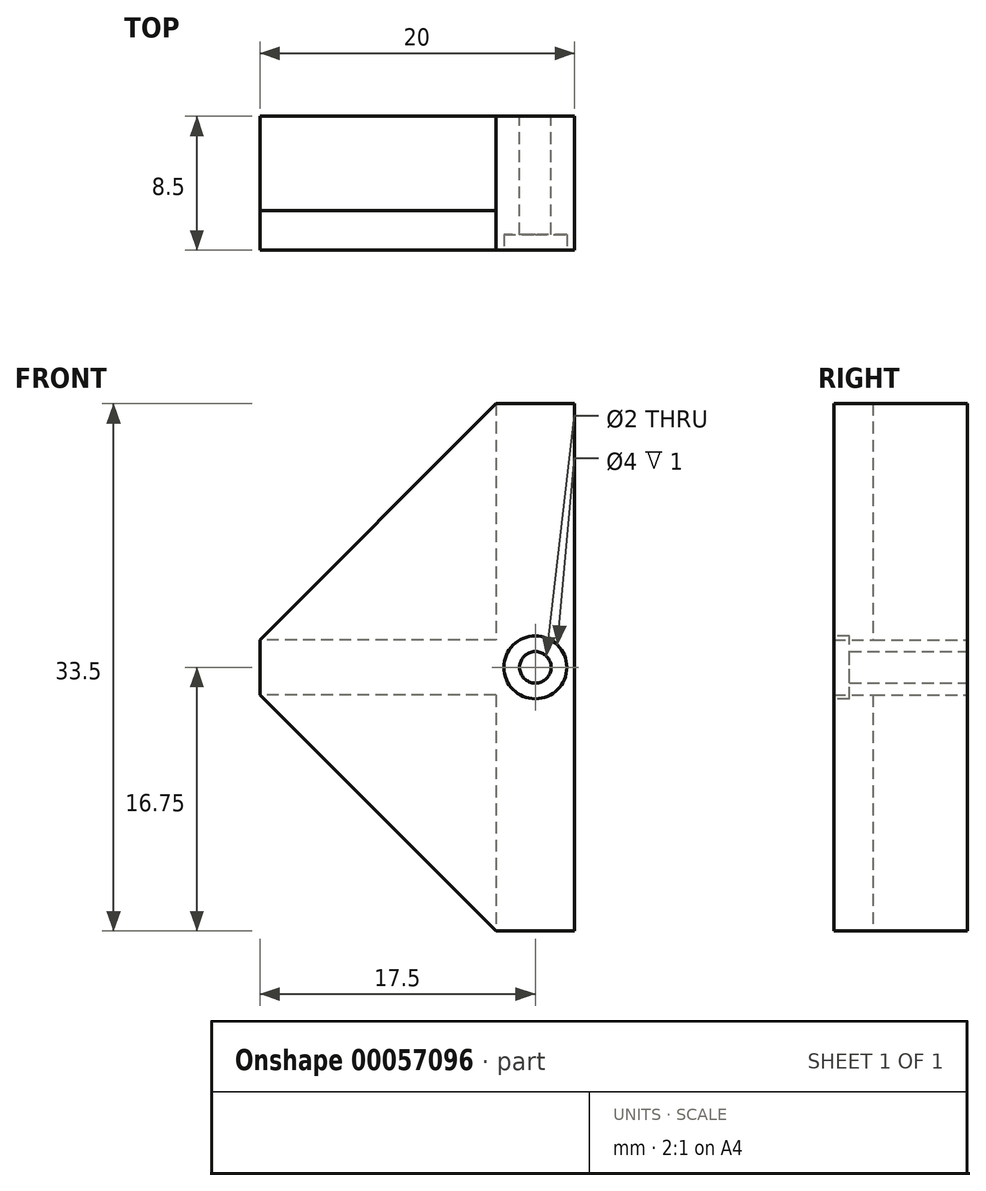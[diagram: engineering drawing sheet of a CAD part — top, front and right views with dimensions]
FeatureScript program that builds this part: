
annotation { "Feature Type Name" : "Feature", "Feature Type Description" : "" }
export const myFeature = defineFeature(function(context is Context, id is Id, definition is map)
    precondition{}
    {
        {
            var Q0;
            Q0=qCreatedBy(makeId("Front.planeOp"),FACE);
            var sketch = newSketch(context, id + "F0", { "sketchPlane" : qUnion([Q0])});
            skLineSegment(sketch, "E0.rect.bottom", {"start": v(2.5, 16.75) * mm, "end": v(-2.5, 16.75) * mm});
            skLineSegment(sketch, "E0.rect.top", {"start": v(2.5, -16.75) * mm, "end": v(-2.5, -16.75) * mm});
            skLineSegment(sketch, "E0.rect.left", {"start": v(2.5, 16.75) * mm, "end": v(2.5, 1) * mm});
            skLineSegment(sketch, "E0.rect.right", {"start": v(-2.5, 16.75) * mm, "end": v(-2.5, 1.75) * mm});
            skPoint(sketch, "E0.rect.middle", {"position": v(0, 0) * mm});
            skLineSegment(sketch, "E1.rect.right", {"start": v(-17.5, 1.75) * mm, "end": v(-17.5, -1.75) * mm});
            skLineSegment(sketch, "E2.trimOffspring", {"start": v(-2.5, -1.75) * mm, "end": v(-2.5, -16.75) * mm});
            skLineSegment(sketch, "E3.trimOffspring", {"start": v(-2.5, -1.75) * mm, "end": v(-17.5, -1.75) * mm});
            skLineSegment(sketch, "E4.trimOffspring", {"start": v(2.5, -2.5) * mm, "end": v(2.5, -16.75) * mm});
            skLineSegment(sketch, "E5.trimOffspring", {"start": v(-2.5, 1.75) * mm, "end": v(-17.5, 1.75) * mm});
            skLineSegment(sketch, "E6", {"start": v(2.5, -2.5) * mm, "end": v(2.5, 1) * mm});
            skSolve(sketch);
        }
        {
            var Q0;
            Q0=qSketchRegion(id+"F0",true);
            extrude(context, id + "F1", {"entities" : qUnion([Q0]), "depth" : 6 * mm});
        }
        {
            var Q0;
            Q0=makeQuery(id+"F1.opExtrude","CAP_FACE",FACE,{"disambiguationData":[OSD([sQuery(id+"F0.wireOp",EDGE,"E0.rect.bottom"),sQuery(id+"F0.wireOp",EDGE,"E0.rect.top"),sQuery(id+"F0.wireOp",EDGE,"E0.rect.left"),sQuery(id+"F0.wireOp",EDGE,"E0.rect.right"),sQuery(id+"F0.wireOp",EDGE,"E1.rect.bottom"),sQuery(id+"F0.wireOp",EDGE,"E1.rect.top"),sQuery(id+"F0.wireOp",EDGE,"E1.rect.left"),sQuery(id+"F0.wireOp",EDGE,"E1.rect.right"),sQuery(id+"F0.wireOp",EDGE,"E2.trimOffspring"),sQuery(id+"F0.wireOp",EDGE,"E3.trimOffspring"),sQuery(id+"F0.wireOp",EDGE,"E4.trimOffspring"),sQuery(id+"F0.wireOp",EDGE,"E5.trimOffspring")])],"isStart":false});
            var sketch = newSketch(context, id + "F2", { "sketchPlane" : qUnion([Q0])});
            skLineSegment(sketch, "E7", {"start": v(-17.5, 1.75) * mm, "end": v(-2.5, 16.75) * mm});
            skLineSegment(sketch, "E8", {"start": v(-2.5, 16.75) * mm, "end": v(0, 16.75) * mm});
            skLineSegment(sketch, "E9", {"start": v(-17.5, 1.75) * mm, "end": v(-17.5, 0) * mm});
            skLineSegment(sketch, "E10.MirrorCS", {"start": v(2.5, 16.75) * mm, "end": v(0, 16.75) * mm});
            skLineSegment(sketch, "E11.MirrorCS", {"start": v(2.5, -16.75) * mm, "end": v(0, -16.75) * mm});
            skLineSegment(sketch, "E12.MirrorCS", {"start": v(-2.5, -16.75) * mm, "end": v(0, -16.75) * mm});
            skLineSegment(sketch, "E13.MirrorCS", {"start": v(-17.5, -1.75) * mm, "end": v(-17.5, 0) * mm});
            skLineSegment(sketch, "E14.MirrorCS", {"start": v(-17.5, -1.75) * mm, "end": v(-2.5, -16.75) * mm});
            skLineSegment(sketch, "E15", {"start": v(2.5, 16.75) * mm, "end": v(2.5, -16.75) * mm});
            skSolve(sketch);
        }
        {
            var Q0;
            Q0=qSketchRegion(id+"F2",true);
            extrude(context, id + "F3", {"entities" : qUnion([Q0]), "operationType" : NewBodyOperationType.ADD, "depth" : 2.5 * mm});
        }
        {
            var Q0;
            Q0=makeQuery(id+"F1.opExtrude","CAP_FACE",FACE,{"disambiguationData":[OSD([sQuery(id+"F0.wireOp",EDGE,"E0.rect.bottom"),sQuery(id+"F0.wireOp",EDGE,"E0.rect.top"),sQuery(id+"F0.wireOp",EDGE,"E0.rect.left"),sQuery(id+"F0.wireOp",EDGE,"E0.rect.right"),sQuery(id+"F0.wireOp",EDGE,"E1.rect.bottom"),sQuery(id+"F0.wireOp",EDGE,"E1.rect.top"),sQuery(id+"F0.wireOp",EDGE,"E1.rect.left"),sQuery(id+"F0.wireOp",EDGE,"E1.rect.right"),sQuery(id+"F0.wireOp",EDGE,"E2.trimOffspring"),sQuery(id+"F0.wireOp",EDGE,"E3.trimOffspring"),sQuery(id+"F0.wireOp",EDGE,"E4.trimOffspring"),sQuery(id+"F0.wireOp",EDGE,"E5.trimOffspring")])],"isStart":true});
            var sketch = newSketch(context, id + "F4", { "sketchPlane" : qUnion([Q0])});
            skCircle(sketch, "E16", {"center": v(0, 0) * mm, "radius": 1 * mm});
            skSolve(sketch);
        }
        {
            var Q0;
            Q0=qSketchRegion(id+"F4",true);
            extrude(context, id + "F5", {"entities" : qUnion([Q0]), "operationType" : NewBodyOperationType.REMOVE, "endBound" : BoundingType.THROUGH_ALL, "oppositeDirection" : true, "depth" : 25 * mm});
        }
        {
            var Q0;
            Q0=makeQuery(id+"F3.opExtrude","CAP_FACE",FACE,{"disambiguationData":[OSD([sQuery(id+"F2.wireOp",EDGE,"E7"),sQuery(id+"F2.wireOp",EDGE,"E8"),sQuery(id+"F2.wireOp",EDGE,"E9"),sQuery(id+"F2.wireOp",EDGE,"E10.MirrorCS"),sQuery(id+"F2.wireOp",EDGE,"E11.MirrorCS"),sQuery(id+"F2.wireOp",EDGE,"E12.MirrorCS"),sQuery(id+"F2.wireOp",EDGE,"E13.MirrorCS"),sQuery(id+"F2.wireOp",EDGE,"E14.MirrorCS"),sQuery(id+"F2.wireOp",EDGE,"E15")])],"isStart":false});
            var sketch = newSketch(context, id + "F6", { "sketchPlane" : qUnion([Q0])});
            skCircle(sketch, "E17", {"center": v(0, 0) * mm, "radius": 2 * mm});
            skSolve(sketch);
        }
        {
            var Q0;
            Q0 = qSketchRegion(id + "F6", true);
            extrude(context, id + "F7", {"entities" : qUnion([Q0]), "operationType" : NewBodyOperationType.REMOVE, "oppositeDirection" : true, "depth" : 1 * mm});
        }
    });
